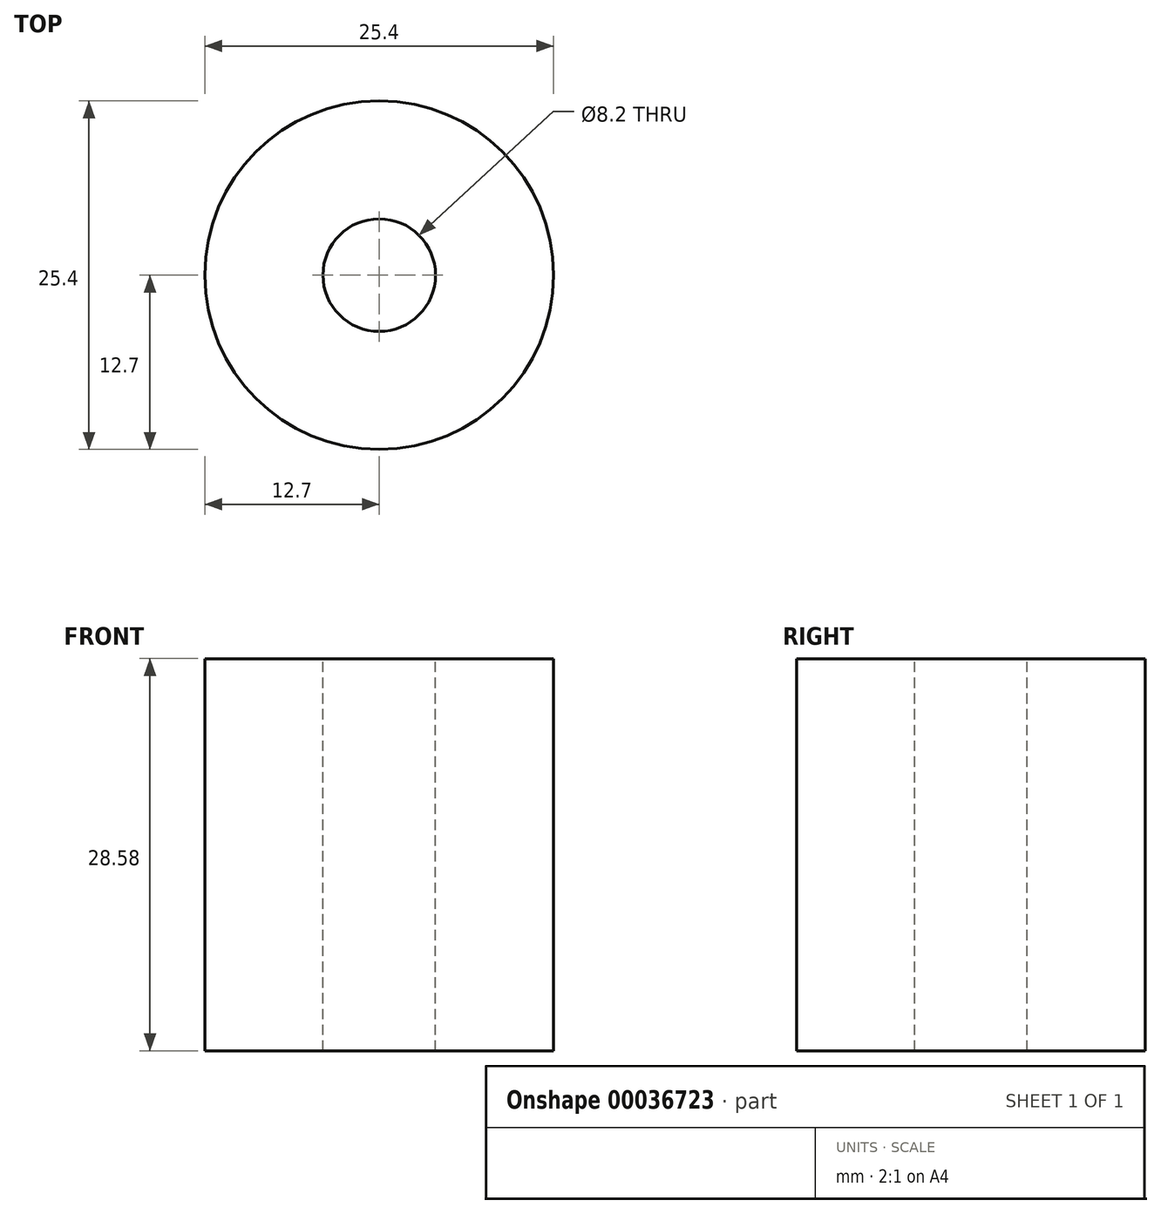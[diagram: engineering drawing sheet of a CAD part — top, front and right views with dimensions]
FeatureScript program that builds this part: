
annotation { "Feature Type Name" : "Feature", "Feature Type Description" : "" }
export const myFeature = defineFeature(function(context is Context, id is Id, definition is map)
    precondition{}
    {
        {
            var Q0;
            Q0=qCreatedBy(makeId("Top.planeOp"),FACE);
            var sketch = newSketch(context, id + "F0", { "sketchPlane" : qUnion([Q0])});
            skCircle(sketch, "E0", {"center": v(0, 0) * mm, "radius": 12.7 * mm});
            skSolve(sketch);
        }
        {
            var Q0;
            Q0=makeQuery(id+"F0.imprint","IMPRINT",FACE,{"disambiguationData":[TD([[makeQuery(id+"F0.imprint","IMPRINT",EDGE,{"derivedFrom":sQuery(id+"F0.wireOp",EDGE,"smO72GXd-D0mf-UbgI-fLAB-JfWzUzAEBpVC.bottom")}),-1.0]])]});
            var Q1;
            Q1=makeQuery(id+"F0.imprint","IMPRINT",FACE,{"disambiguationData":[TD([[makeQuery(id+"F0.imprint","IMPRINT",EDGE,{"derivedFrom":sQuery(id+"F0.wireOp",EDGE,"E0")}),1.0]])]});
            extrude(context, id + "F1", {"entities" : qUnion([Q0, Q1]), "depth" : 28.57 * mm, "offsetDistance" : 25.4 * mm});
        }
        {
            var Q0;
            Q0=makeQuery(id+"F1.opExtrude","CAP_FACE",FACE,{"disambiguationData":[OSD([sQuery(id+"F0.wireOp",EDGE,"E0")])],"isStart":false});
            var sketch = newSketch(context, id + "F2", { "sketchPlane" : qUnion([Q0])});
            skPoint(sketch, "E1", {"position": v(0, 0) * mm});
            skSolve(sketch);
        }
        {
            var Q0;
            Q0=sQuery(id+"F2.wireOp",VERTEX,"E1");
            var Q1;
            Q1=makeQuery(id+"F1.opExtrude","SWEPT_BODY",BODY,{"disambiguationData":[OSD([sQuery(id+"F0.wireOp",EDGE,"E0")])]});
            hole(context, id + "F3", {"style" : HoleStyle.SIMPLE, "endStyle" : HoleEndStyle.THROUGH, "standardTappedOrClearance" : lookupTablePath({ "standard" : "ANSI", "fit" : "Close", "size" : "5/16", "type" : "Clearance" }), "standardBlindInLast" : lookupTablePath({ "fit" : "Close", "standard" : "ANSI", "size" : "5/16", "type" : "Clearance" }), "holeDiameter" : 8.2 * mm, "majorDiameter" : 6.35 * mm, "tappedDepth" : 12.7 * mm, "tapClearance" : 3, "locations" : qUnion([Q0]), "scope" : qUnion([Q1])});
        }
    });
